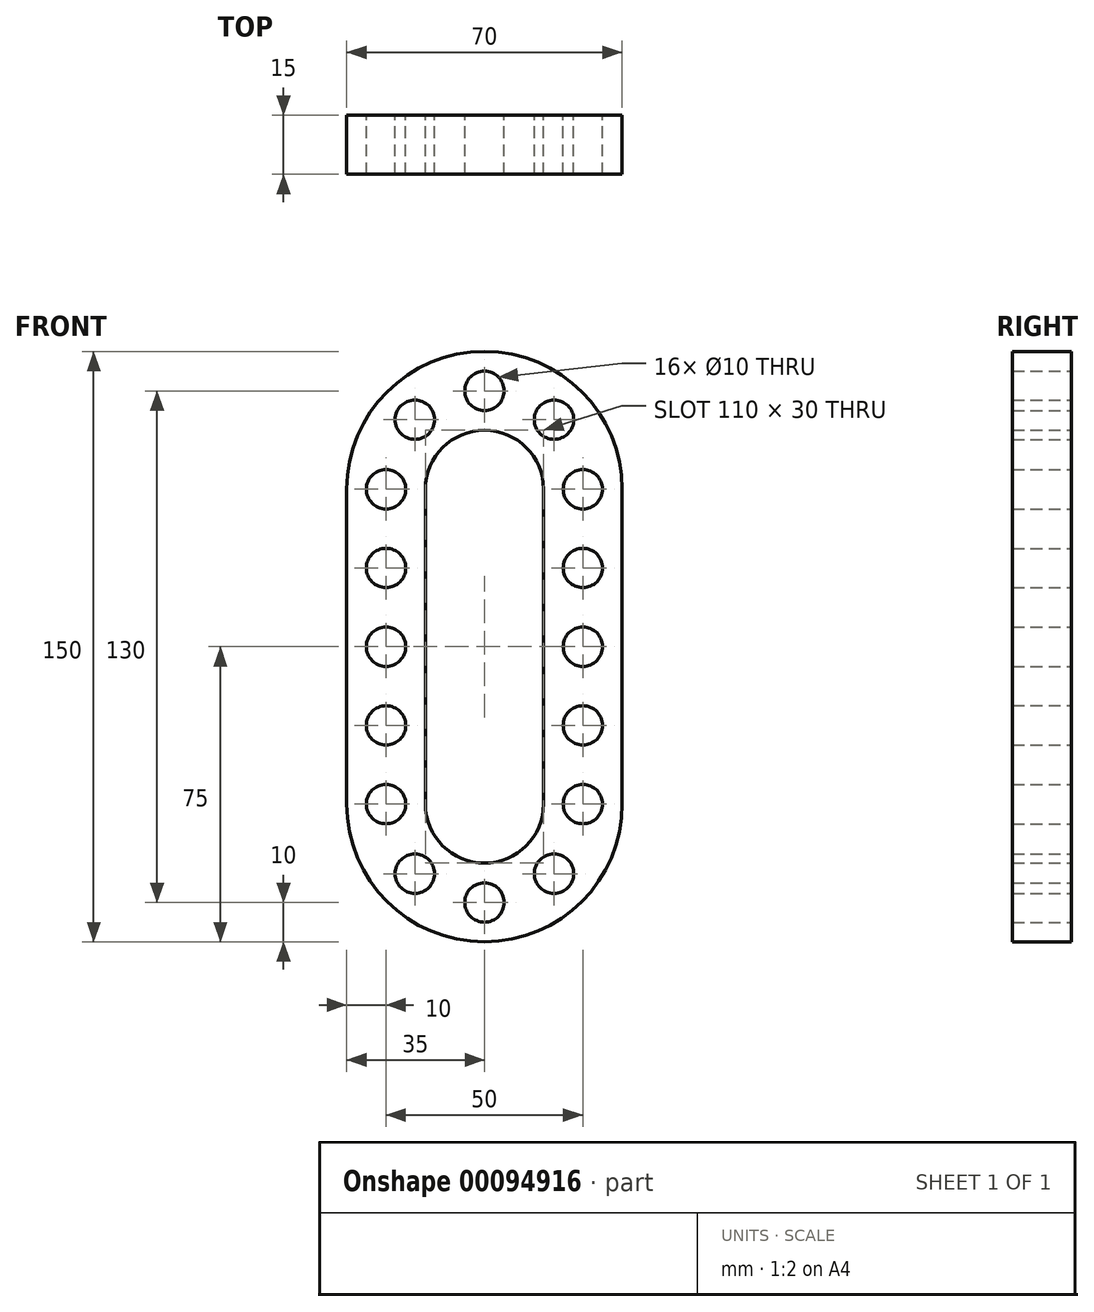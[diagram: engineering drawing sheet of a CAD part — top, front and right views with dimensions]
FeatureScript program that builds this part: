
annotation { "Feature Type Name" : "Feature", "Feature Type Description" : "" }
export const myFeature = defineFeature(function(context is Context, id is Id, definition is map)
    precondition{}
    {
        {
            var Q0;
            Q0=qCreatedBy(makeId("Front.planeOp"),FACE);
            var sketch = newSketch(context, id + "F0", { "sketchPlane" : qUnion([Q0])});
            skPoint(sketch, "E0", {"position": v(-35, 40) * mm});
            skLineSegment(sketch, "E1", {"start": v(-35, 40) * mm, "end": v(-35, 0) * mm});
            skArc(sketch, "E2", {"start": v(0, 75) * mm, "mid": v(-24.75, 64.75) * mm, "end": v(-35, 40) * mm});
            skArc(sketch, "E3", {"start": v(0, 55) * mm, "mid": v(-10.6, 50.6) * mm, "end": v(-15, 40) * mm});
            skLineSegment(sketch, "E4", {"start": v(-15, 40) * mm, "end": v(-15, 0) * mm});
            skCircle(sketch, "E5", {"center": v(-25, 40) * mm, "radius": 5 * mm});
            skCircle(sketch, "E6.1.0", {"center": v(-17.68, 57.68) * mm, "radius": 5 * mm});
            skCircle(sketch, "E6.2.0", {"center": v(0, 65) * mm, "radius": 5 * mm});
            skLineSegment(sketch, "E6.anchor1", {"start": v(0, 40) * mm, "end": v(-25, 40) * mm, "construction": true});
            skLineSegment(sketch, "E6.anchor2", {"start": v(0, 40) * mm, "end": v(0, 65) * mm, "construction": true});
            skCircle(sketch, "E7.0.1.0", {"center": v(-25, 20) * mm, "radius": 5 * mm});
            skCircle(sketch, "E7.0.2.0", {"center": v(-25, 0) * mm, "radius": 5 * mm});
            skLineSegment(sketch, "E7.direction1", {"start": v(-25, 40) * mm, "end": v(0, 40) * mm, "construction": true});
            skLineSegment(sketch, "E7.direction2", {"start": v(-25, 40) * mm, "end": v(-25, 20) * mm, "construction": true});
            skLineSegment(sketch, "E8.MirrorCS", {"start": v(25, 40) * mm, "end": v(25, 20) * mm, "construction": true});
            skCircle(sketch, "E9.MirrorC", {"center": v(17.68, 57.68) * mm, "radius": 5 * mm});
            skPoint(sketch, "E10.MirrorP", {"position": v(35, 40) * mm});
            skCircle(sketch, "E11.MirrorC", {"center": v(25, 20) * mm, "radius": 5 * mm});
            skCircle(sketch, "E12.MirrorC", {"center": v(25, 40) * mm, "radius": 5 * mm});
            skArc(sketch, "E13.MirrorCS", {"start": v(0, 55) * mm, "mid": v(10.6, 50.6) * mm, "end": v(15, 40) * mm});
            skLineSegment(sketch, "E14.MirrorCS", {"start": v(15, 40) * mm, "end": v(15, 0) * mm});
            skArc(sketch, "E15.MirrorCS", {"start": v(0, 75) * mm, "mid": v(24.75, 64.75) * mm, "end": v(35, 40) * mm});
            skLineSegment(sketch, "E16.MirrorCS", {"start": v(35, 40) * mm, "end": v(35, 0) * mm});
            skCircle(sketch, "E17.MirrorC", {"center": v(25, 0) * mm, "radius": 5 * mm});
            skLineSegment(sketch, "E18.MirrorCS", {"start": v(0, -40) * mm, "end": v(-25, -40) * mm, "construction": true});
            skCircle(sketch, "E19.MirrorC", {"center": v(25, -40) * mm, "radius": 5 * mm});
            skLineSegment(sketch, "E20.MirrorCS", {"start": v(15, -40) * mm, "end": v(15, 0) * mm});
            skLineSegment(sketch, "E21.MirrorCS", {"start": v(35, -40) * mm, "end": v(35, 0) * mm});
            skArc(sketch, "E22.MirrorCS", {"start": v(0, -75) * mm, "mid": v(24.75, -64.75) * mm, "end": v(35, -40) * mm});
            skPoint(sketch, "E23.MirrorP", {"position": v(-35, -40) * mm});
            skLineSegment(sketch, "E24.MirrorCS", {"start": v(25, -40) * mm, "end": v(25, -20) * mm, "construction": true});
            skArc(sketch, "E25.MirrorCS", {"start": v(0, -55) * mm, "mid": v(10.6, -50.6) * mm, "end": v(15, -40) * mm});
            skLineSegment(sketch, "E26.MirrorCS", {"start": v(0, -40) * mm, "end": v(0, -65) * mm, "construction": true});
            skLineSegment(sketch, "E27.MirrorCS", {"start": v(-25, -40) * mm, "end": v(0, -40) * mm, "construction": true});
            skArc(sketch, "E28.MirrorCS", {"start": v(0, -75) * mm, "mid": v(-24.75, -64.75) * mm, "end": v(-35, -40) * mm});
            skLineSegment(sketch, "E29.MirrorCS", {"start": v(-25, -40) * mm, "end": v(-25, -20) * mm, "construction": true});
            skCircle(sketch, "E30.MirrorC", {"center": v(-25, -20) * mm, "radius": 5 * mm});
            skLineSegment(sketch, "E31.MirrorCS", {"start": v(-35, -40) * mm, "end": v(-35, 0) * mm});
            skCircle(sketch, "E32.MirrorC", {"center": v(-25, -40) * mm, "radius": 5 * mm});
            skCircle(sketch, "E33.MirrorC", {"center": v(17.68, -57.68) * mm, "radius": 5 * mm});
            skPoint(sketch, "E34.MirrorP", {"position": v(35, -40) * mm});
            skCircle(sketch, "E35.MirrorC", {"center": v(0, -65) * mm, "radius": 5 * mm});
            skCircle(sketch, "E36.MirrorC", {"center": v(25, -20) * mm, "radius": 5 * mm});
            skArc(sketch, "E37.MirrorCS", {"start": v(0, -55) * mm, "mid": v(-10.6, -50.6) * mm, "end": v(-15, -40) * mm});
            skLineSegment(sketch, "E38.MirrorCS", {"start": v(-15, -40) * mm, "end": v(-15, 0) * mm});
            skCircle(sketch, "E39.MirrorC", {"center": v(-17.68, -57.68) * mm, "radius": 5 * mm});
            skSolve(sketch);
        }
        {
            var Q0;
            Q0 = qSketchRegion(id + "F0", true);
            extrude(context, id + "F1", {"entities" : qUnion([Q0]), "depth" : 15 * mm});
        }
    });
